# Revit family: Opal Support Rail 600 STR
name_source: partatom
category: Plumbing Fixtures
revit_build: Autodesk Revit 2016 (Build: 20161004_0715(x64)
units: mm (PartAtom-declared; Revit-internal decimal feet)

## family parameters
Cut with Voids When Loaded = No
Host = Face
OmniClass Number = 23.40.20.21.47
OmniClass Title = Bath Grab Bars
Part Type = Normal
Room Calculation Point = No
Round Connector Dimension = Use Radius
Shared = No

## types (3) — shared parameters
Assembly Code = C1030200
CW Connection = No
HW Connection = No
Manufacturer = GWA Bathrooms & Kitchens
Material_Base = GWA_Metal-Stainless
Rail_Height = 75 mm
URL = https://www.caroma.com.au
Vent Connection = No
Waste Connection = No
zero-valued in all types: Default Elevation

## per-type parameters (varying)
| type | Description | Model | Rail_Width |
| OPAL SUPPORT RAIL 300 STR | Opal Support Rail 300 STR | 687375C | 300 mm |
| OPAL SUPPORT RAIL 450 STR | Opal Support Rail 450 STR | 687376C | 450 mm  [stored 1.47638 ft] |
| OPAL SUPPORT RAIL 600 STR | Opal Support Rail 600 STR | 687377C | 600 mm  [stored 1.9685 ft] |

note: [stored X ft] marks values corroborated as IEEE doubles in the binary element streams (Revit-internal decimal feet)

## geometry (parser evidence)
native form markers: Sweep x2
no freeform markers — native parametric forms only
